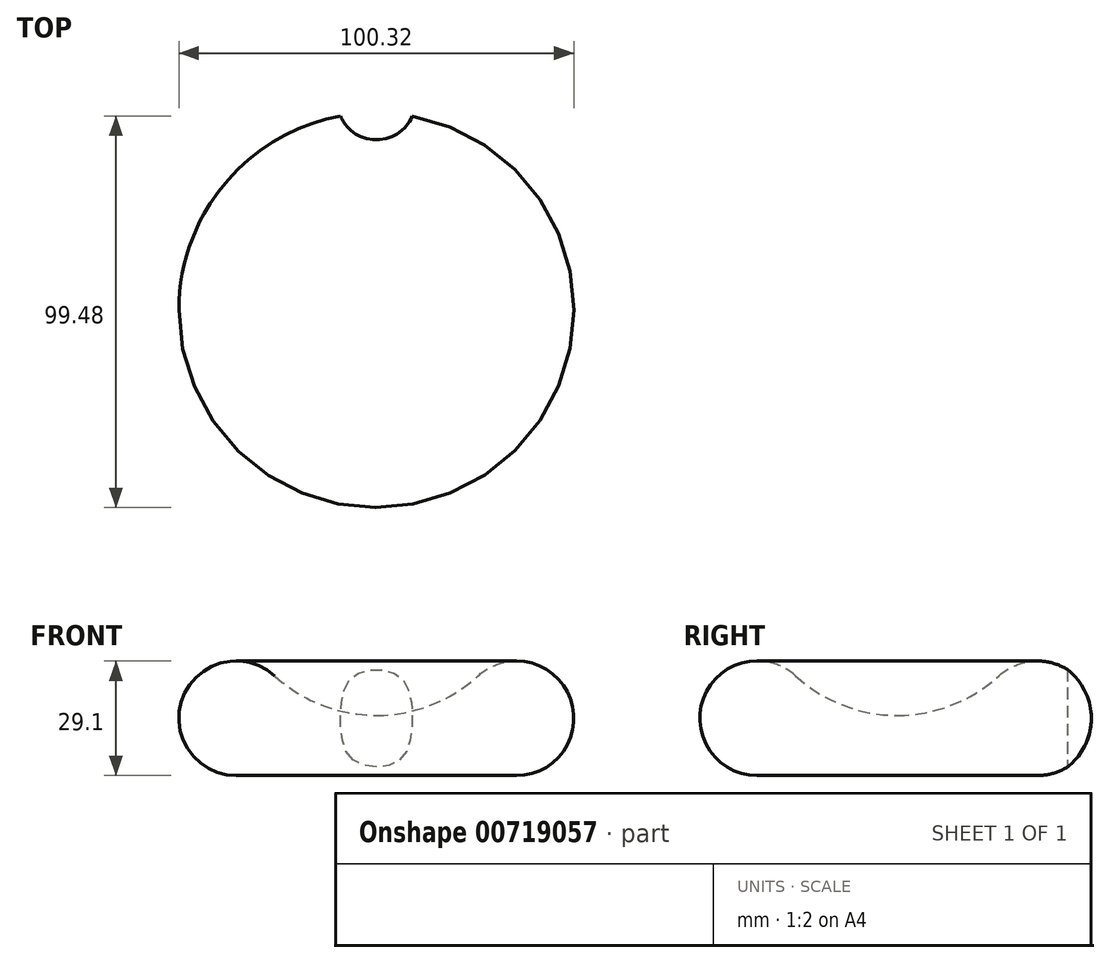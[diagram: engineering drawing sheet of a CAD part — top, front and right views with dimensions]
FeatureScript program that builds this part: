
annotation { "Feature Type Name" : "Feature", "Feature Type Description" : "" }
export const myFeature = defineFeature(function(context is Context, id is Id, definition is map)
    precondition{}
    {
        {
            var Q0;
            Q0=qCreatedBy(makeId("Front.planeOp"),FACE);
            var sketch = newSketch(context, id + "F0", { "sketchPlane" : qUnion([Q0])});
            skArc(sketch, "E0", {"start": v(-25.8, 25.3) * mm, "mid": v(-13.83, 17.89) * mm, "end": v(0, 15.3) * mm});
            skArc(sketch, "E1", {"start": v(-25.8, 25.3) * mm, "mid": v(-49.17, 19.81) * mm, "end": v(-35.6, 0) * mm});
            skLineSegment(sketch, "E2", {"start": v(0, 0) * mm, "end": v(-35.6, 0) * mm});
            skLineSegment(sketch, "E3", {"start": v(0, 0) * mm, "end": v(0, 15.3) * mm});
            skSolve(sketch);
        }
        {
            var Q0;
            Q0 = qSketchRegion(id + "F0", true);
            var Q1;
            Q1=sQuery(id+"F0.wireOp",EDGE,"E3");
            revolve(context, id + "F1", {"surfaceOperationType" : NewSurfaceOperationType.NEW, "entities" : qUnion([Q0]), "axis" : qUnion([Q1]), "revolveType" : RevolveType.FULL});
        }
        {
            var Q0;
            Q0=qCreatedBy(makeId("Top.planeOp"),FACE);
            var sketch = newSketch(context, id + "F2", { "sketchPlane" : qUnion([Q0])});
            skCircle(sketch, "E4", {"center": v(0, 53.11) * mm, "radius": 9.89 * mm});
            skSolve(sketch);
        }
        {
            var Q0;
            Q0=makeQuery(id+"F2.imprint","IMPRINT",FACE,{"disambiguationData":[TD([[makeQuery(id+"F2.imprint","IMPRINT",EDGE,{"derivedFrom":sQuery(id+"F2.wireOp",EDGE,"E4")}),1.0]])]});
            extrude(context, id + "F3", {"entities" : qUnion([Q0]), "operationType" : NewBodyOperationType.REMOVE, "depth" : 38.9 * mm, "offsetDistance" : 25 * mm});
        }
    });
